# Revit family: Dali Side Chair
name_source: partatom
category: Furniture
revit_build: Autodesk Revit 2017 (Build: 20160225_1515(x64)
units: mm (PartAtom-declared; Revit-internal decimal feet)

## family parameters
Always vertical = Yes
Cut with Voids When Loaded = No
OmniClass Number = 23.40.20.00
OmniClass Title = General Furniture and Specialties
Room Calculation Point = No
Shared = No
Work Plane-Based = No

## types (1)
- Dali Side Chair
    Assembly Code = E2020200
    Assistance = Call for assistance number: 336.941.3446
    Chair type = Side
    Collection = Dali
    Depth = 19 mm
    Description = Wood seat and legs available in mix wood and metal
    Height = 34 mm
    Industry = Café, Restaurant, Bistro, Hotel, Club, College
    Manufacturer = Beaufurn
    Manufacturer Country = USA
    Metal = Standard aluminum, white and black
    Model = Dali Side Chair
    Products of collection = Dali Side Chair Laminate, Pad, Uph, Pronto and Barstool Wood Veneer, Laminate, Papped Seat, Upholstered, Pronto
    Seat height = 18 mm  [stored 0.0590551 ft]
    Type Comments = Ideal for Cafeteria, Church, Dining, Hospitality, Institutional, Office, University
    URL = https://beaufurn.com
    Usage = Indoor
    Width = 17 mm
    Wood = Standard wood finishes or COF
    Yardage = 0

note: [stored X ft] marks values corroborated as IEEE doubles in the binary element streams (Revit-internal decimal feet)
